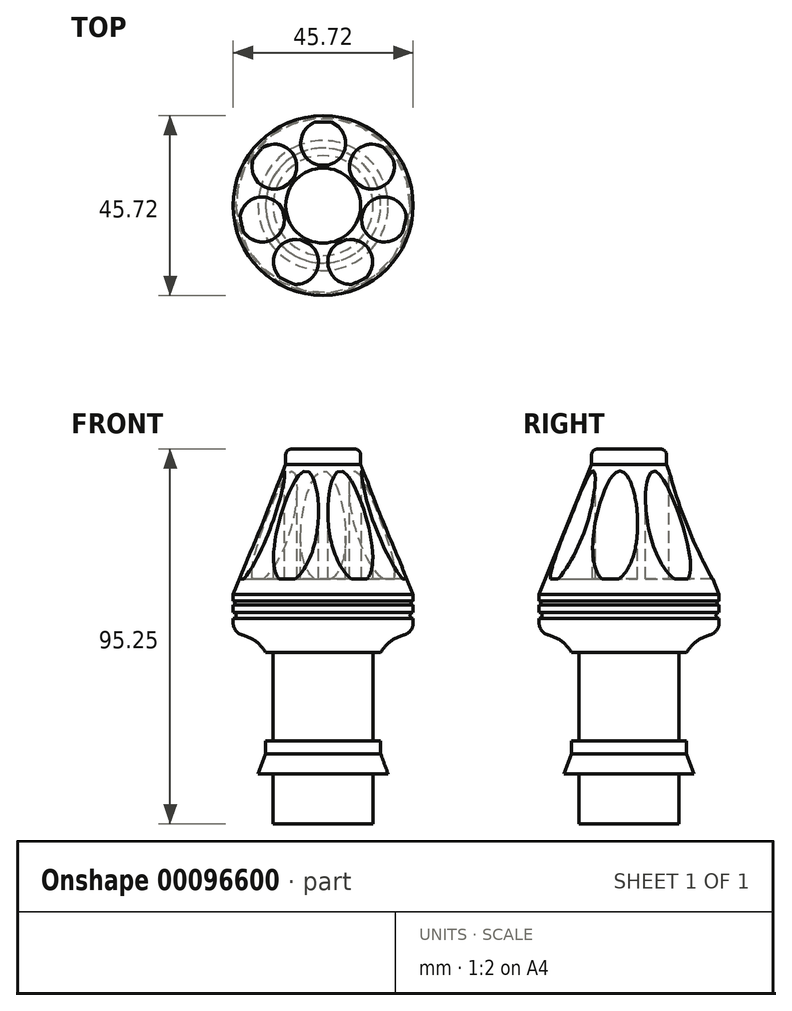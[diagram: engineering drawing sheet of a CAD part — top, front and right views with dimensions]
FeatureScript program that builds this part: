
annotation { "Feature Type Name" : "Feature", "Feature Type Description" : "" }
export const myFeature = defineFeature(function(context is Context, id is Id, definition is map)
    precondition{}
    {
        {
            var Q0;
            Q0=qCreatedBy(makeId("Front.planeOp"),FACE);
            var sketch = newSketch(context, id + "F0", { "sketchPlane" : qUnion([Q0])});
            skLineSegment(sketch, "E0", {"start": v(0, 115.95) * mm, "end": v(0, -88.18) * mm, "construction": true});
            skLineSegment(sketch, "E1", {"start": v(12.7, 0) * mm, "end": v(0, 0) * mm});
            skLineSegment(sketch, "E2", {"start": v(14.6, 17.83) * mm, "end": v(16.51, 12.7) * mm});
            skArc(sketch, "E3", {"start": v(20.45, 47.97) * mm, "mid": v(17.07, 46.36) * mm, "end": v(14.6, 43.56) * mm});
            skPoint(sketch, "E4.visualSharp", {"position": v(24.13, 48.13) * mm});
            skArc(sketch, "E4.filletArc", {"start": v(20.45, 47.97) * mm, "mid": v(22.18, 49.1) * mm, "end": v(22.86, 51.05) * mm});
            skLineSegment(sketch, "E5", {"start": v(0, 95.25) * mm, "end": v(0, 0) * mm});
            skLineSegment(sketch, "E6", {"start": v(8, 95.25) * mm, "end": v(0, 95.25) * mm});
            skLineSegment(sketch, "E7", {"start": v(16.51, 12.7) * mm, "end": v(12.7, 12.7) * mm});
            skLineSegment(sketch, "E8", {"start": v(12.7, 12.7) * mm, "end": v(12.7, 0) * mm});
            skLineSegment(sketch, "E9", {"start": v(14.6, 17.83) * mm, "end": v(14.6, 21.13) * mm});
            skLineSegment(sketch, "E10", {"start": v(14.6, 21.13) * mm, "end": v(12.7, 21.13) * mm});
            skLineSegment(sketch, "E11", {"start": v(12.7, 21.13) * mm, "end": v(12.7, 43.56) * mm});
            skLineSegment(sketch, "E12", {"start": v(12.7, 43.56) * mm, "end": v(14.6, 43.56) * mm});
            skLineSegment(sketch, "E13", {"start": v(9.52, 93.73) * mm, "end": v(9.52, 91.29) * mm});
            skPoint(sketch, "E14.visualSharp", {"position": v(9.52, 95.25) * mm});
            skArc(sketch, "E14.filletArc", {"start": v(9.52, 93.73) * mm, "mid": v(9.08, 94.8) * mm, "end": v(8, 95.25) * mm});
            skLineSegment(sketch, "E15", {"start": v(9.52, 91.29) * mm, "end": v(22.86, 58.28) * mm});
            skLineSegment(sketch, "E16", {"start": v(22.86, 51.05) * mm, "end": v(22.86, 58.28) * mm});
            skArc(sketch, "E17", {"start": v(22.86, 56.62) * mm, "mid": v(22.35, 56.11) * mm, "end": v(22.86, 55.6) * mm});
            skArc(sketch, "E18", {"start": v(22.86, 53.75) * mm, "mid": v(22.1, 52.98) * mm, "end": v(22.86, 52.22) * mm});
            skSolve(sketch);
        }
        {
            var Q0;
            Q0=makeQuery(id+"F0.imprint","IMPRINT",FACE,{"disambiguationData":[TD([[makeQuery(id+"F0.imprint","IMPRINT",EDGE,{"derivedFrom":sQuery(id+"F0.wireOp",EDGE,"E1")}),-1.0]])]});
            var Q1;
            Q1=sQuery(id+"F0.wireOp",EDGE,"E0");
            revolve(context, id + "F1", {"surfaceOperationType" : NewSurfaceOperationType.NEW, "entities" : qUnion([Q0]), "axis" : qUnion([Q1]), "revolveType" : RevolveType.FULL});
        }
        {
            var Q0;
            Q0=makeQuery(id+"F1.opRevolve","SWEPT_FACE",FACE,{"disambiguationData":[OSD([sQuery(id+"F0.wireOp",EDGE,"E6")])]});
            var sketch = newSketch(context, id + "F2", { "sketchPlane" : qUnion([Q0])});
            skCircle(sketch, "E19", {"center": v(0, 0) * mm, "radius": 15.88 * mm});
            skCircle(sketch, "E20", {"center": v(0, 15.88) * mm, "radius": 5.72 * mm});
            skCircle(sketch, "E21.1.0", {"center": v(-12.41, 9.9) * mm, "radius": 5.72 * mm});
            skCircle(sketch, "E21.2.0", {"center": v(-15.48, -3.53) * mm, "radius": 5.72 * mm});
            skCircle(sketch, "E21.3.0", {"center": v(-6.89, -14.3) * mm, "radius": 5.72 * mm});
            skCircle(sketch, "E21.4.0", {"center": v(6.89, -14.3) * mm, "radius": 5.72 * mm});
            skCircle(sketch, "E21.5.0", {"center": v(15.48, -3.53) * mm, "radius": 5.72 * mm});
            skCircle(sketch, "E21.6.0", {"center": v(12.41, 9.9) * mm, "radius": 5.72 * mm});
            skSolve(sketch);
        }
        {
            var Q0;
            {var subQ0=sQuery(id+"F2.wireOp",EDGE,"E20");var subQ1=sQuery(id+"F2.wireOp",EDGE,"E19");var subQ2=makeQuery(id+"F2.imprint","INTERSECT",VERTEX,{"disambiguationData":[OD(0.0)],"derivedFrom":[subQ1,subQ0]});Q0=makeQuery(id+"F2.imprint","IMPRINT",FACE,{"disambiguationData":[TD([[makeQuery(id+"F2.imprint","IMPRINT",EDGE,{"disambiguationData":[TD([[subQ2,-1.0]])],"derivedFrom":subQ1}),-1.0]])]});}
            var Q1;
            {var subQ0=sQuery(id+"F2.wireOp",EDGE,"E20");var subQ1=sQuery(id+"F2.wireOp",EDGE,"E19");var subQ2=makeQuery(id+"F2.imprint","INTERSECT",VERTEX,{"disambiguationData":[OD(0.0)],"derivedFrom":[subQ1,subQ0]});Q1=makeQuery(id+"F2.imprint","IMPRINT",FACE,{"disambiguationData":[TD([[makeQuery(id+"F2.imprint","IMPRINT",EDGE,{"disambiguationData":[TD([[subQ2,-1.0]])],"derivedFrom":subQ1}),1.0]])]});}
            var Q2;
            {var subQ0=sQuery(id+"F2.wireOp",EDGE,"E21.1.0");var subQ1=sQuery(id+"F2.wireOp",EDGE,"E19");var subQ2=makeQuery(id+"F2.imprint","INTERSECT",VERTEX,{"disambiguationData":[OD(0.0)],"derivedFrom":[subQ1,subQ0]});Q2=makeQuery(id+"F2.imprint","IMPRINT",FACE,{"disambiguationData":[TD([[makeQuery(id+"F2.imprint","IMPRINT",EDGE,{"disambiguationData":[TD([[subQ2,-1.0]])],"derivedFrom":subQ1}),-1.0]])]});}
            var Q3;
            {var subQ0=sQuery(id+"F2.wireOp",EDGE,"E21.1.0");var subQ1=sQuery(id+"F2.wireOp",EDGE,"E19");var subQ2=makeQuery(id+"F2.imprint","INTERSECT",VERTEX,{"disambiguationData":[OD(0.0)],"derivedFrom":[subQ1,subQ0]});Q3=makeQuery(id+"F2.imprint","IMPRINT",FACE,{"disambiguationData":[TD([[makeQuery(id+"F2.imprint","IMPRINT",EDGE,{"disambiguationData":[TD([[subQ2,-1.0]])],"derivedFrom":subQ1}),1.0]])]});}
            var Q4;
            {var subQ0=sQuery(id+"F2.wireOp",EDGE,"E21.3.0");var subQ1=sQuery(id+"F2.wireOp",EDGE,"E19");var subQ2=makeQuery(id+"F2.imprint","INTERSECT",VERTEX,{"disambiguationData":[OD(0.0)],"derivedFrom":[subQ1,subQ0]});Q4=makeQuery(id+"F2.imprint","IMPRINT",FACE,{"disambiguationData":[TD([[makeQuery(id+"F2.imprint","IMPRINT",EDGE,{"disambiguationData":[TD([[subQ2,-1.0]])],"derivedFrom":subQ1}),1.0]])]});}
            var Q5;
            {var subQ0=sQuery(id+"F2.wireOp",EDGE,"E21.3.0");var subQ1=sQuery(id+"F2.wireOp",EDGE,"E19");var subQ2=makeQuery(id+"F2.imprint","INTERSECT",VERTEX,{"disambiguationData":[OD(0.0)],"derivedFrom":[subQ1,subQ0]});Q5=makeQuery(id+"F2.imprint","IMPRINT",FACE,{"disambiguationData":[TD([[makeQuery(id+"F2.imprint","IMPRINT",EDGE,{"disambiguationData":[TD([[subQ2,-1.0]])],"derivedFrom":subQ1}),-1.0]])]});}
            var Q6;
            {var subQ0=sQuery(id+"F2.wireOp",EDGE,"E21.4.0");var subQ1=sQuery(id+"F2.wireOp",EDGE,"E19");var subQ2=makeQuery(id+"F2.imprint","INTERSECT",VERTEX,{"disambiguationData":[OD(0.0)],"derivedFrom":[subQ1,subQ0]});Q6=makeQuery(id+"F2.imprint","IMPRINT",FACE,{"disambiguationData":[TD([[makeQuery(id+"F2.imprint","IMPRINT",EDGE,{"disambiguationData":[TD([[subQ2,-1.0]])],"derivedFrom":subQ1}),1.0]])]});}
            var Q7;
            {var subQ0=sQuery(id+"F2.wireOp",EDGE,"E21.4.0");var subQ1=sQuery(id+"F2.wireOp",EDGE,"E19");var subQ2=makeQuery(id+"F2.imprint","INTERSECT",VERTEX,{"disambiguationData":[OD(0.0)],"derivedFrom":[subQ1,subQ0]});Q7=makeQuery(id+"F2.imprint","IMPRINT",FACE,{"disambiguationData":[TD([[makeQuery(id+"F2.imprint","IMPRINT",EDGE,{"disambiguationData":[TD([[subQ2,-1.0]])],"derivedFrom":subQ1}),-1.0]])]});}
            var Q8;
            {var subQ0=sQuery(id+"F2.wireOp",EDGE,"E21.5.0");var subQ1=sQuery(id+"F2.wireOp",EDGE,"E19");var subQ2=makeQuery(id+"F2.imprint","INTERSECT",VERTEX,{"disambiguationData":[OD(0.0)],"derivedFrom":[subQ1,subQ0]});Q8=makeQuery(id+"F2.imprint","IMPRINT",FACE,{"disambiguationData":[TD([[makeQuery(id+"F2.imprint","IMPRINT",EDGE,{"disambiguationData":[TD([[subQ2,1.0]])],"derivedFrom":subQ1}),1.0]])]});}
            var Q9;
            {var subQ0=sQuery(id+"F2.wireOp",EDGE,"E21.5.0");var subQ1=sQuery(id+"F2.wireOp",EDGE,"E19");var subQ2=makeQuery(id+"F2.imprint","INTERSECT",VERTEX,{"disambiguationData":[OD(0.0)],"derivedFrom":[subQ1,subQ0]});Q9=makeQuery(id+"F2.imprint","IMPRINT",FACE,{"disambiguationData":[TD([[makeQuery(id+"F2.imprint","IMPRINT",EDGE,{"disambiguationData":[TD([[subQ2,1.0]])],"derivedFrom":subQ1}),-1.0]])]});}
            var Q10;
            {var subQ0=sQuery(id+"F2.wireOp",EDGE,"E21.6.0");var subQ1=sQuery(id+"F2.wireOp",EDGE,"E19");var subQ2=makeQuery(id+"F2.imprint","INTERSECT",VERTEX,{"disambiguationData":[OD(0.0)],"derivedFrom":[subQ1,subQ0]});Q10=makeQuery(id+"F2.imprint","IMPRINT",FACE,{"disambiguationData":[TD([[makeQuery(id+"F2.imprint","IMPRINT",EDGE,{"disambiguationData":[TD([[subQ2,-1.0]])],"derivedFrom":subQ1}),-1.0]])]});}
            var Q11;
            {var subQ0=sQuery(id+"F2.wireOp",EDGE,"E21.6.0");var subQ1=sQuery(id+"F2.wireOp",EDGE,"E19");var subQ2=makeQuery(id+"F2.imprint","INTERSECT",VERTEX,{"disambiguationData":[OD(0.0)],"derivedFrom":[subQ1,subQ0]});Q11=makeQuery(id+"F2.imprint","IMPRINT",FACE,{"disambiguationData":[TD([[makeQuery(id+"F2.imprint","IMPRINT",EDGE,{"disambiguationData":[TD([[subQ2,-1.0]])],"derivedFrom":subQ1}),1.0]])]});}
            var Q12;
            {var subQ0=sQuery(id+"F2.wireOp",EDGE,"E21.2.0");var subQ1=sQuery(id+"F2.wireOp",EDGE,"E19");var subQ2=makeQuery(id+"F2.imprint","INTERSECT",VERTEX,{"disambiguationData":[OD(0.0)],"derivedFrom":[subQ1,subQ0]});Q12=makeQuery(id+"F2.imprint","IMPRINT",FACE,{"disambiguationData":[TD([[makeQuery(id+"F2.imprint","IMPRINT",EDGE,{"disambiguationData":[TD([[subQ2,-1.0]])],"derivedFrom":subQ1}),-1.0]])]});}
            var Q13;
            {var subQ0=sQuery(id+"F2.wireOp",EDGE,"E21.2.0");var subQ1=sQuery(id+"F2.wireOp",EDGE,"E19");var subQ2=makeQuery(id+"F2.imprint","INTERSECT",VERTEX,{"disambiguationData":[OD(0.0)],"derivedFrom":[subQ1,subQ0]});Q13=makeQuery(id+"F2.imprint","IMPRINT",FACE,{"disambiguationData":[TD([[makeQuery(id+"F2.imprint","IMPRINT",EDGE,{"disambiguationData":[TD([[subQ2,-1.0]])],"derivedFrom":subQ1}),1.0]])]});}
            extrude(context, id + "F3", {"entities" : qUnion([Q0, Q1, Q2, Q3, Q4, Q5, Q6, Q7, Q8, Q9, Q10, Q11, Q12, Q13]), "operationType" : NewBodyOperationType.REMOVE, "oppositeDirection" : true, "depth" : 33.02 * mm, "offsetDistance" : 25.4 * mm});
        }
    });
